# Revit family: IS_Mavone_Multiproduct_BIM_FR_T0050;T0051;T0052
name_source: partatom
category: Plumbing Fixtures
revit_build: Autodesk Revit 2017 (Build: 20160225_1515(x64)
units: mm (PartAtom-declared; Revit-internal decimal feet)

## family parameters
Cut with Voids When Loaded = No
Host = Face
OmniClass Number = 23.45.05.14
OmniClass Title = Plumbing Fixtures - Sanitary Washing Units
Part Type = Normal
Room Calculation Point = No
Round Connector Dimension = Use Diameter
Shared = Yes

## types (9) — shared parameters
Accessoires = www.idealstandard.be
Assembly Code = C1030200
Auteur = Ideal Standard
CodeBarre = 0
ConseilsDInstallation = www.idealstandard.be
DateDeCréation = 2018_08_15
Default Elevation = 900 mm  [stored 2.95276 ft]
Espace = Interne
Forme = Rectangulaire
Handle = SOT_Sottini_Fittings_Chrome_Render
IfcExportAs = IfcFurnitureType
IfcExportType = USERDEFINED
InformationsProduit = www.idealstandard.be
LienUtile = www.idealstandard.be
Longueur = 440 mm  [stored 1.44357 ft]
MainColor = White
Manufacturer = www.idealstandard.be
Marque = Ideal Standard
Raccordement = Plomberie
URL = www.idealstandard.be
Uniclass2015Code = Pr_40_30_78_04
Uniclass2015Title = Bathroom integrated duct work
Uniclass2015Version = Products v1.1
UnitéDeMesure = millimeters
UnitéDeTemps = an
UnitéMonétaire = Euro
UrlDuFabricant = www.idealstandard.be
zero-valued in all types: CWFU, Cost, CoûtDeRemplacement, HWFU, Profondeur, WFU

## per-type parameters (varying)
| type | Bim-NomDuProjet | Caractéristiques | Couleur | Description | Finition | Hauteur | Laminate | Largeur | Model | Révision |
| T0050OV - Mavone 600mm wall hung vanity unit - 2 drawers - Gloss White | ISI_IdealStandard_Furniture_Mavone_T0050OV | MEUBLE DEUX TIROIRS 600x440 BLANC LAQUE | Blanc laqué | MEUBLE DEUX TIROIRS 600x440 BLANC LAQUE | Blanc laqué | 490 mm | SOT_Sottini_Laminate_White_OV_Render | 600 mm | T0050OV | T0050OV |
| T0051OV - Mavone 800mm wall hung vanity unit - 2 drawers - Gloss White | ISI_IdealStandard_Furniture_Mavone_T0051OV | MEUBLE DEUX TIROIRS 800x440 BLANC LAQUE | Blanc laqué | MEUBLE DEUX TIROIRS 800x440 BLANC LAQUE | Blanc laqué | 490 mm | SOT_Sottini_Laminate_White_OV_Render | 800 mm  [stored 2.62467 ft] | T0051OV | T0051OV |
| T0052OV - Mavone 1000mm wall hung vanity unit - 2 drawers - Gloss White | ISI_IdealStandard_Furniture_Mavone_T0052OV | MEUBLE DEUX TIROIRS 1000x440 BLANC LAQUE | Blanc laqué | MEUBLE DEUX TIROIRS 1000x440 BLANC LAQUE | Blanc laqué | 490 mm | SOT_Sottini_Laminate_White_OV_Render | 1000 mm  [stored 3.28084 ft] | T0052OV | T0052OV |
| T0050PH - Mavone 600mm wall hung vanity unit - 2 drawers - Gloss Light Grey | ISI_IdealStandard_Furniture_Mavone_T0050PH | MEUBLE DEUX TIROIRS 600x440 GRIS PLUME BRILLANT | Gris plume brillant | MEUBLE DEUX TIROIRS 600x440 GRIS PLUME BRILLANT | Gris plume brillant | 490 mm | SOT_Sottini_Laminate_GlossLightGrey_PH_Render | 600 mm | T0050PH | T0050PH |
| T0050VI - Mavone 600mm wall hung vanity unit - 2 drawers - Light Wood | ISI_IdealStandard_Furniture_Mavone_T0050VI | MEUBLE DEUX TIROIRS 600x440 BOIS NATUREL | Bois naturel | MEUBLE DEUX TIROIRS 600x440 BOIS NATUREL | Bois naturel | 490 mm | SOT_Sottini_Laminate_LightWood_VI_Render | 600 mm | T0050VI | T0050VI |
| T0051PH - Mavone 800mm wall hung vanity unit - 2 drawers - Gloss Light Grey | ISI_IdealStandard_Furniture_Mavone_T0051PH | MEUBLE DEUX TIROIRS 800x440 GRIS PLUME BRILLANT | Gris plume brillant | MEUBLE DEUX TIROIRS 800x440 GRIS PLUME BRILLANT | Gris plume brillant | 490 mm | SOT_Sottini_Laminate_GlossLightGrey_PH_Render | 800 mm  [stored 2.62467 ft] | T0051PH | T0051PH |
| T0051VI - Mavone 800mm wall hung vanity unit - 2 drawers - Light Wood | ISI_IdealStandard_Furniture_Mavone_T0051VI | MEUBLE DEUX TIROIRS 800x440 BOIS NATUREL | Bois naturel | MEUBLE DEUX TIROIRS 800x440 BOIS NATUREL | Bois naturel | 490 mm | SOT_Sottini_Laminate_LightWood_VI_Render | 800 mm  [stored 2.62467 ft] | T0051VI | T0051VI |
| T0052PH - Mavone 1000mm wall hung vanity unit - 2 drawers - Gloss Light Grey | ISI_IdealStandard_Furniture_Mavone_T0052PH | MEUBLE DEUX TIROIRS 1000x440 GRIS PLUME BRILLANT | Gris plume brillant | MEUBLE DEUX TIROIRS 1000x440 GRIS PLUME BRILLANT | Gris plume brillant | 440 mm  [stored 1.44357 ft] | SOT_Sottini_Laminate_GlossLightGrey_PH_Render | 1000 mm  [stored 3.28084 ft] | T0052PH | T0052PH |
| T0052VI - Mavone 1000mm wall hung vanity unit - 2 drawers - Light Wood | ISI_IdealStandard_Furniture_Mavone_T0052VI | MEUBLE DEUX TIROIRS 1000x440 BOIS NATUREL | Bois naturel | MEUBLE DEUX TIROIRS 1000x440 BOIS NATUREL | Bois naturel | 490 mm | SOT_Sottini_Laminate_LightWood_VI_Render | 1000 mm  [stored 3.28084 ft] | T0052VI | T0052VI |

note: [stored X ft] marks values corroborated as IEEE doubles in the binary element streams (Revit-internal decimal feet)

## geometry (parser evidence)
native form markers: Sweep x3
no freeform markers — native parametric forms only
